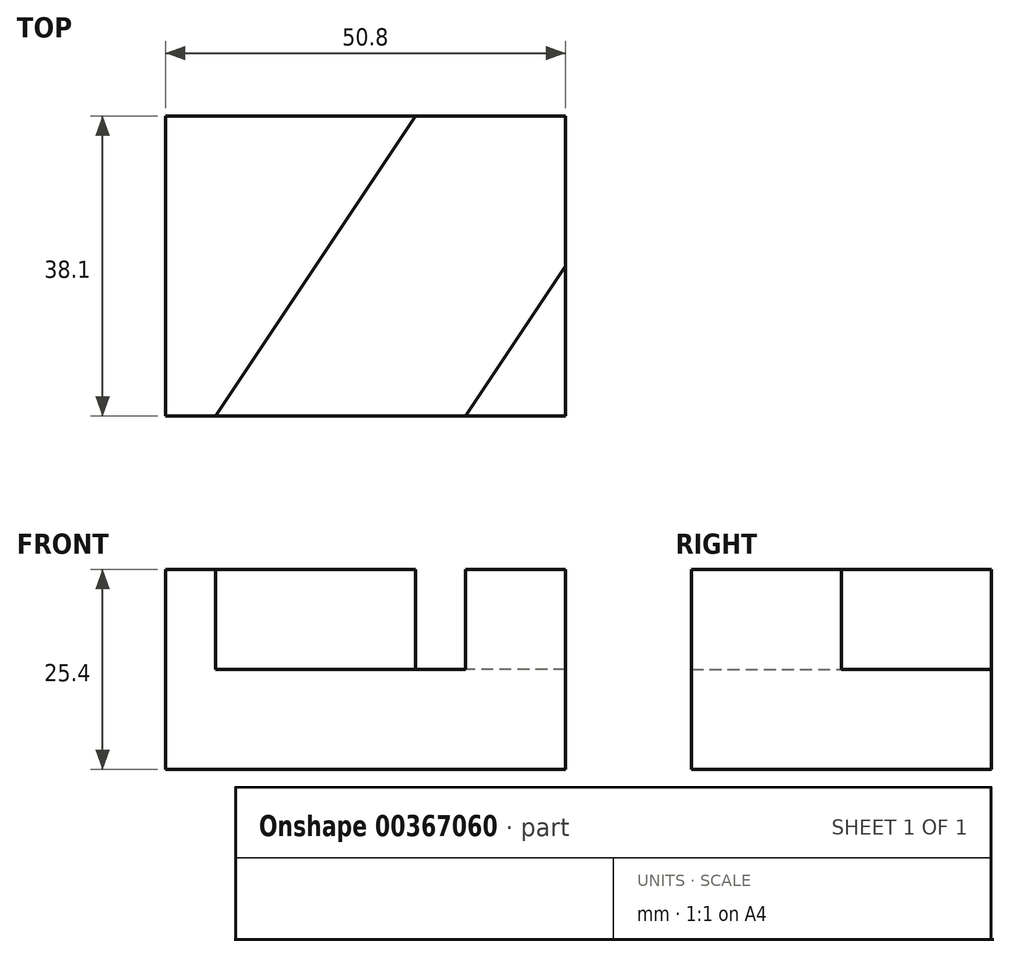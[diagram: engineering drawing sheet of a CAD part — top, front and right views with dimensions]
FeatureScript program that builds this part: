
annotation { "Feature Type Name" : "Feature", "Feature Type Description" : "" }
export const myFeature = defineFeature(function(context is Context, id is Id, definition is map)
    precondition{}
    {
        {
            var Q0;
            Q0=qCreatedBy(makeId("Front.planeOp"),FACE);
            var sketch = newSketch(context, id + "F0", { "sketchPlane" : qUnion([Q0])});
            skLineSegment(sketch, "E0", {"start": v(-50.8, 23.5) * mm, "end": v(-50.8, -1.9) * mm});
            skLineSegment(sketch, "E1", {"start": v(-50.8, -1.9) * mm, "end": v(0, -1.9) * mm});
            skLineSegment(sketch, "E2", {"start": v(0, -1.9) * mm, "end": v(0, 23.5) * mm});
            skLineSegment(sketch, "E3", {"start": v(0, 23.5) * mm, "end": v(-50.8, 23.5) * mm});
            skSolve(sketch);
        }
        {
            var Q0;
            Q0=makeQuery(id+"F0.imprint","IMPRINT",FACE,{"disambiguationData":[TD([[makeQuery(id+"F0.imprint","IMPRINT",EDGE,{"derivedFrom":sQuery(id+"F0.wireOp",EDGE,"E0")}),1.0]])]});
            extrude(context, id + "F1", {"entities" : qUnion([Q0]), "depth" : 38.1 * mm});
        }
        {
            var Q0;
            Q0=makeQuery(id+"F1.opExtrude","SWEPT_FACE",FACE,{"disambiguationData":[OSD([sQuery(id+"F0.wireOp",EDGE,"E3")])]});
            var sketch = newSketch(context, id + "F2", { "sketchPlane" : qUnion([Q0])});
            skLineSegment(sketch, "E4", {"start": v(-44.45, -38.1) * mm, "end": v(-19.05, 0) * mm});
            skLineSegment(sketch, "E5", {"start": v(-19.05, 0) * mm, "end": v(-50.8, 0) * mm});
            skLineSegment(sketch, "E6", {"start": v(-50.8, 0) * mm, "end": v(-50.8, -38.1) * mm});
            skLineSegment(sketch, "E7", {"start": v(-50.8, -38.1) * mm, "end": v(-44.45, -38.1) * mm});
            skLineSegment(sketch, "E8", {"start": v(-12.7, -38.1) * mm, "end": v(0, -38.1) * mm});
            skLineSegment(sketch, "E9", {"start": v(0, -38.1) * mm, "end": v(0, -19.05) * mm});
            skLineSegment(sketch, "E10", {"start": v(0, -19.05) * mm, "end": v(-12.7, -38.1) * mm});
            skLineSegment(sketch, "E11", {"start": v(0, 0) * mm, "end": v(0, -19.05) * mm});
            skLineSegment(sketch, "E12", {"start": v(-12.7, -38.1) * mm, "end": v(-44.45, -38.1) * mm});
            skLineSegment(sketch, "E13", {"start": v(-44.45, -38.1) * mm, "end": v(-12.7, -38.1) * mm});
            skLineSegment(sketch, "E14", {"start": v(0, -19.05) * mm, "end": v(0, 0) * mm});
            skLineSegment(sketch, "E15", {"start": v(-19.05, 0) * mm, "end": v(-44.45, -38.1) * mm});
            skSolve(sketch);
        }
        {
            var Q0;
            Q0=makeQuery(id+"F2.imprint","IMPRINT",FACE,{"disambiguationData":[TD([[makeQuery(id+"F2.imprint","IMPRINT",EDGE,{"derivedFrom":sQuery(id+"F2.wireOp",EDGE,"E10")}),-1.0]])]});
            extrude(context, id + "F3", {"entities" : qUnion([Q0]), "operationType" : NewBodyOperationType.REMOVE, "oppositeDirection" : true, "depth" : 12.7 * mm});
        }
    });
